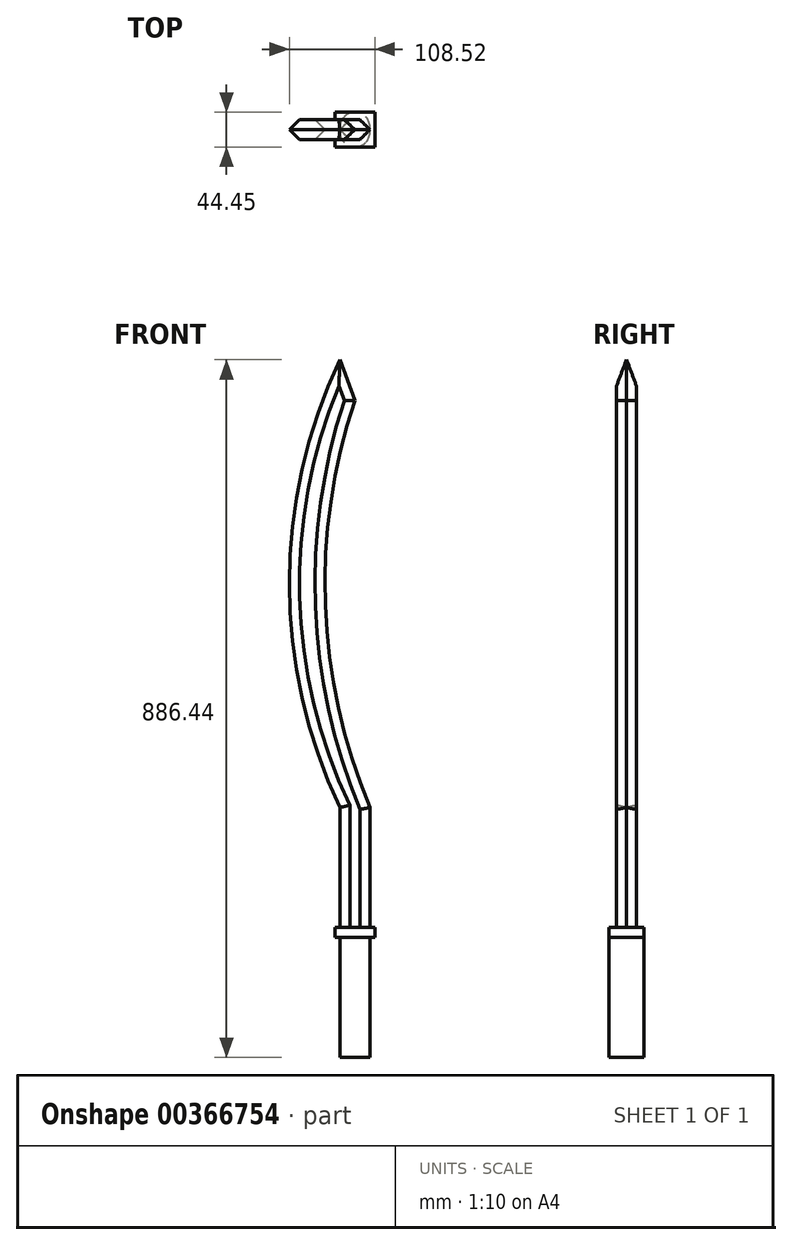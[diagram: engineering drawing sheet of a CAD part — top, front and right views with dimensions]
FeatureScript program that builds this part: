
annotation { "Feature Type Name" : "Feature", "Feature Type Description" : "" }
export const myFeature = defineFeature(function(context is Context, id is Id, definition is map)
    precondition{}
    {
        {
            var Q0;
            Q0=qCreatedBy(makeId("Front.planeOp"),FACE);
            var sketch = newSketch(context, id + "F0", { "sketchPlane" : qUnion([Q0])});
            skLineSegment(sketch, "E0", {"start": v(0, -44.01) * mm, "end": v(-19.05, -44.01) * mm});
            skLineSegment(sketch, "E1", {"start": v(-19.05, -44.01) * mm, "end": v(-19.05, 108.39) * mm});
            skLineSegment(sketch, "E2.MirrorCS", {"start": v(0, -44.01) * mm, "end": v(19.05, -44.01) * mm});
            skLineSegment(sketch, "E3.MirrorCS", {"start": v(19.05, -44.01) * mm, "end": v(19.05, 108.39) * mm});
            skLineSegment(sketch, "E4", {"start": v(-19.05, 108.39) * mm, "end": v(19.05, 108.39) * mm});
            skSolve(sketch);
        }
        {
            var Q0;
            Q0 = qSketchRegion(id + "F0", true);
            extrude(context, id + "F1", {"entities" : qUnion([Q0]), "depth" : 44.45 * mm});
        }
        {
            var Q0;
            Q0=makeQuery(id+"F1.opExtrude","CAP_FACE",FACE,{"disambiguationData":[OSD([sQuery(id+"F0.wireOp",EDGE,"E0"),sQuery(id+"F0.wireOp",EDGE,"E1"),sQuery(id+"F0.wireOp",EDGE,"E2.MirrorCS"),sQuery(id+"F0.wireOp",EDGE,"E3.MirrorCS"),sQuery(id+"F0.wireOp",EDGE,"E4")])],"isStart":false});
            var sketch = newSketch(context, id + "F2", { "sketchPlane" : qUnion([Q0])});
            skLineSegment(sketch, "E5", {"start": v(-19.05, 108.39) * mm, "end": v(-25.4, 108.39) * mm});
            skLineSegment(sketch, "E6", {"start": v(19.05, 108.39) * mm, "end": v(25.4, 108.39) * mm});
            skLineSegment(sketch, "E7", {"start": v(-25.4, 108.39) * mm, "end": v(-25.4, 121.09) * mm});
            skLineSegment(sketch, "E8", {"start": v(25.4, 108.39) * mm, "end": v(25.4, 121.09) * mm});
            skLineSegment(sketch, "E9", {"start": v(-25.4, 121.09) * mm, "end": v(25.4, 121.09) * mm});
            skSolve(sketch);
        }
        {
            var Q0;
            Q0=makeQuery(id+"F2.imprint","IMPRINT",FACE,{"disambiguationData":[TD([[makeQuery(id+"F2.imprint","IMPRINT",EDGE,{"derivedFrom":sQuery(id+"F2.wireOp",EDGE,"E5")}),-1.0]])]});
            extrude(context, id + "F3", {"entities" : qUnion([Q0]), "operationType" : NewBodyOperationType.ADD, "depth" : -44.45 * mm});
        }
        {
            var Q0;
            {var subQ0=sQuery(id+"F0.wireOp",EDGE,"E4");Q0=makeQuery(id+"F3.boolean.opBoolean","MERGE",FACE,{"derivedFrom":[makeQuery(id+"F1.opExtrude","CAP_FACE",FACE,{"disambiguationData":[OSD([sQuery(id+"F0.wireOp",EDGE,"E0"),sQuery(id+"F0.wireOp",EDGE,"E1"),sQuery(id+"F0.wireOp",EDGE,"E2.MirrorCS"),sQuery(id+"F0.wireOp",EDGE,"E3.MirrorCS"),subQ0])],"isStart":false}),makeQuery(id+"F3.opExtrude","CAP_FACE",FACE,{"disambiguationData":[OSD([subQ0,sQuery(id+"F2.wireOp",EDGE,"E5"),sQuery(id+"F2.wireOp",EDGE,"E6"),sQuery(id+"F2.wireOp",EDGE,"E7"),sQuery(id+"F2.wireOp",EDGE,"E8"),sQuery(id+"F2.wireOp",EDGE,"E9")])],"isStart":true})]});}
            var sketch = newSketch(context, id + "F4", { "sketchPlane" : qUnion([Q0])});
            skLineSegment(sketch, "E10", {"start": v(-19.05, 108.39) * mm, "end": v(-19.05, 273.49) * mm});
            skLineSegment(sketch, "E11", {"start": v(19.05, 108.39) * mm, "end": v(19.05, 273.49) * mm});
            skArc(sketch, "E12", {"start": v(-19.05, 842.43) * mm, "mid": v(-83.12, 557.96) * mm, "end": v(-19.05, 273.49) * mm});
            skArc(sketch, "E13", {"start": v(0, 790.78) * mm, "mid": v(-37.5, 530.4) * mm, "end": v(19.05, 273.49) * mm});
            skLineSegment(sketch, "E14", {"start": v(-19.05, 842.43) * mm, "end": v(0, 790.78) * mm});
            skSolve(sketch);
        }
        {
            var Q0;
            Q0 = qSketchRegion(id + "F4", true);
            var Q1;
            {var subQ6=sQuery(id+"F4.wireOp",EDGE,"E12");Q1=makeQuery(id+"F4.imprint","IMPRINT",FACE,{"disambiguationData":[TD([[makeQuery(id+"F4.imprint","IMPRINT",EDGE,{"derivedFrom":subQ6}),1.0]])]});}
            extrude(context, id + "F5", {"entities" : qUnion([Q0, Q1]), "operationType" : NewBodyOperationType.ADD, "depth" : -34.92 * mm, "hasSecondDirection" : true, "secondDirectionOppositeDirection" : true, "secondDirectionDepth" : 9.52 * mm});
        }
        {
            var Q0;
            Q0=makeQuery(id+"F1.opExtrude","CAP_EDGE",EDGE,{"disambiguationData":[OSD([sQuery(id+"F0.wireOp",EDGE,"E3.MirrorCS")])],"isStart":true});
            var Q1;
            Q1=makeQuery(id+"F1.opExtrude","CAP_EDGE",EDGE,{"disambiguationData":[OSD([sQuery(id+"F0.wireOp",EDGE,"E3.MirrorCS")])],"isStart":false});
            var Q2;
            Q2=makeQuery(id+"F1.opExtrude","CAP_EDGE",EDGE,{"disambiguationData":[OSD([sQuery(id+"F0.wireOp",EDGE,"E1")])],"isStart":false});
            var Q3;
            Q3=makeQuery(id+"F1.opExtrude","CAP_EDGE",EDGE,{"disambiguationData":[OSD([sQuery(id+"F0.wireOp",EDGE,"E1")])],"isStart":true});
            fillet(context, id + "F6", {"entities" : qUnion([Q0, Q1, Q2, Q3]), "radius" : 19.05 * mm, "tangentPropagation" : true, "allowEdgeOverflow" : false});
        }
        {
            var Q0;
            Q0=makeQuery(id+"F5.opExtrude","CAP_EDGE",EDGE,{"disambiguationData":[OSD([sQuery(id+"F4.wireOp",EDGE,"E13")])],"isStart":true});
            var Q1;
            Q1=makeQuery(id+"F5.opExtrude","CAP_EDGE",EDGE,{"disambiguationData":[OSD([sQuery(id+"F4.wireOp",EDGE,"E13")])],"isStart":false});
            var Q2;
            Q2=makeQuery(id+"F5.opExtrude","CAP_EDGE",EDGE,{"disambiguationData":[OSD([sQuery(id+"F4.wireOp",EDGE,"E12")])],"isStart":true});
            var Q3;
            Q3=makeQuery(id+"F5.opExtrude","CAP_EDGE",EDGE,{"disambiguationData":[OSD([sQuery(id+"F4.wireOp",EDGE,"E12")])],"isStart":false});
            var Q4;
            Q4=makeQuery(id+"F5.opExtrude","CAP_EDGE",EDGE,{"disambiguationData":[OSD([sQuery(id+"F4.wireOp",EDGE,"E14")])],"isStart":true});
            var Q5;
            Q5=makeQuery(id+"F5.opExtrude","CAP_EDGE",EDGE,{"disambiguationData":[OSD([sQuery(id+"F4.wireOp",EDGE,"E14")])],"isStart":false});
            var Q6;
            Q6=makeQuery(id+"F5.opExtrude","CAP_EDGE",EDGE,{"disambiguationData":[OSD([sQuery(id+"F4.wireOp",EDGE,"E10")])],"isStart":true});
            var Q7;
            Q7=makeQuery(id+"F5.opExtrude","CAP_EDGE",EDGE,{"disambiguationData":[OSD([sQuery(id+"F4.wireOp",EDGE,"E10")])],"isStart":false});
            var Q8;
            Q8=makeQuery(id+"F5.opExtrude","CAP_EDGE",EDGE,{"disambiguationData":[OSD([sQuery(id+"F4.wireOp",EDGE,"E11")])],"isStart":true});
            var Q9;
            Q9=makeQuery(id+"F5.opExtrude","CAP_EDGE",EDGE,{"disambiguationData":[OSD([sQuery(id+"F4.wireOp",EDGE,"E11")])],"isStart":false});
            chamfer(context, id + "F7", {"entities" : qUnion([Q0, Q1, Q2, Q3, Q4, Q5, Q6, Q7, Q8, Q9]), "chamferType" : ChamferType.OFFSET_ANGLE, "width" : 12.7 * mm, "oppositeDirection" : false, "angle" : 45 * degree, "tangentPropagation" : true});
        }
    });
